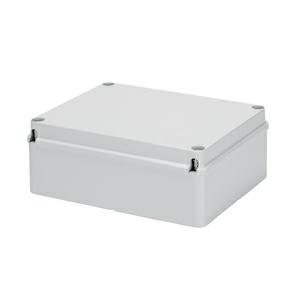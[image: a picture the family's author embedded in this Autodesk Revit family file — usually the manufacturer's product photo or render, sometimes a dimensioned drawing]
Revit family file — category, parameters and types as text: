
# Revit family: Building-SurfaceMountingEnclosures-GEWISS-44CE-JUNCTION-BOXES-WALL-MOUNTING
name_source: partatom
category: Apparecchi elettrici
revit_build: Autodesk Revit 2016 (Build: 20161004_0715(x64)
units: mm (PartAtom-declared; Revit-internal decimal feet)

## family parameters
Condiviso = No
Host = Superficie
Mantenere orientamento annotazione = Sì
Numero OmniClass = 23.80.30.14.24
Punto di calcolo locali = Sì
Quota connettore circolare = Usa diametro
Taglio con vuoti quando caricato = No
Tipo di parte = Normale
Titolo OmniClass = Junction Boxes

## types (1)
- Building-SurfaceMountingEnclosures-GEWISS-44CE-JUNCTION-BOXES-WALL-MOUNTING
    Accessories for insulation restoring = GW44621
    Application = Industrial uses
    Carico apparente = 0 VA
    Catalogue = BUILDING
    Catalogue Range = 44 CE
    Classificazione = Other
    Colour = Grey RAL 7035
    Coperchio = GEWISS COPERCHIO TRASPARENTE
    Descrizione = ENCLOSURE W.TRANSP.LID 460X380X120 IP56
    Dettaglio = Eemento di dettaglio - 44CE : 460x380x120
    EAN code = 8011564014145
    Electrocod = 0231
    Glow Wire Test = 650°C
    IDF = 2f48c751-3916-45a0-a840-afda0dddd5b2
    IDT = 9d7720fb-e677-4d26-8d25-fa01e92eaf96
    IP degree = IP56
    Immagine tipo = GW44431.jpg
    Insulation class = II (according to IEC 61140 standards)
    Internal dim. LxHxD (mm) = 460x380x120
    Larghezza_interna = 460 mm  [stored 1.50919 ft]
    Lid = Plain screwed
    Lid colour = Transparent
    Lid screws (no. and type) = 6 insul. sealable hinged
    Lunghezza_interna = 380 mm
    Material = Technopolymer GWPLAST 120
    Max Ã˜ holes possible = 48MM
    Modello = GW44431
    Operating temperature = -25 +60 °C
    Produttore = GEWISS S.p.A.
    Prospetto di default = 1219 mm
    SEO = Box
    Scatola = GW - Grigio RAL 7035
    Shock resistance = IK08
    Spessore = 120 mm  [stored 0.393701 ft]
    Technical sheet = https://www.gewiss.com
    Thermo-pressure with ball = 110
    Torque screws tightening = 1,8NM
    Type of material = Halogen-free in compliance with EN 60754-2
    URL = https://www.gewiss.com
    Version file RFA = 18.0
    Voltaggio = 0 V
    Walls = Smooth

note: source unit labels omitted for Thermo-pressure with ball — the stored unit's dimension contradicts the parameter name (converter mislabeling)

note: [stored X ft] marks values corroborated as IEEE doubles in the binary element streams (Revit-internal decimal feet)

## geometry (parser evidence)
native form markers: Blend x4, Sweep x2
no freeform markers — native parametric forms only
